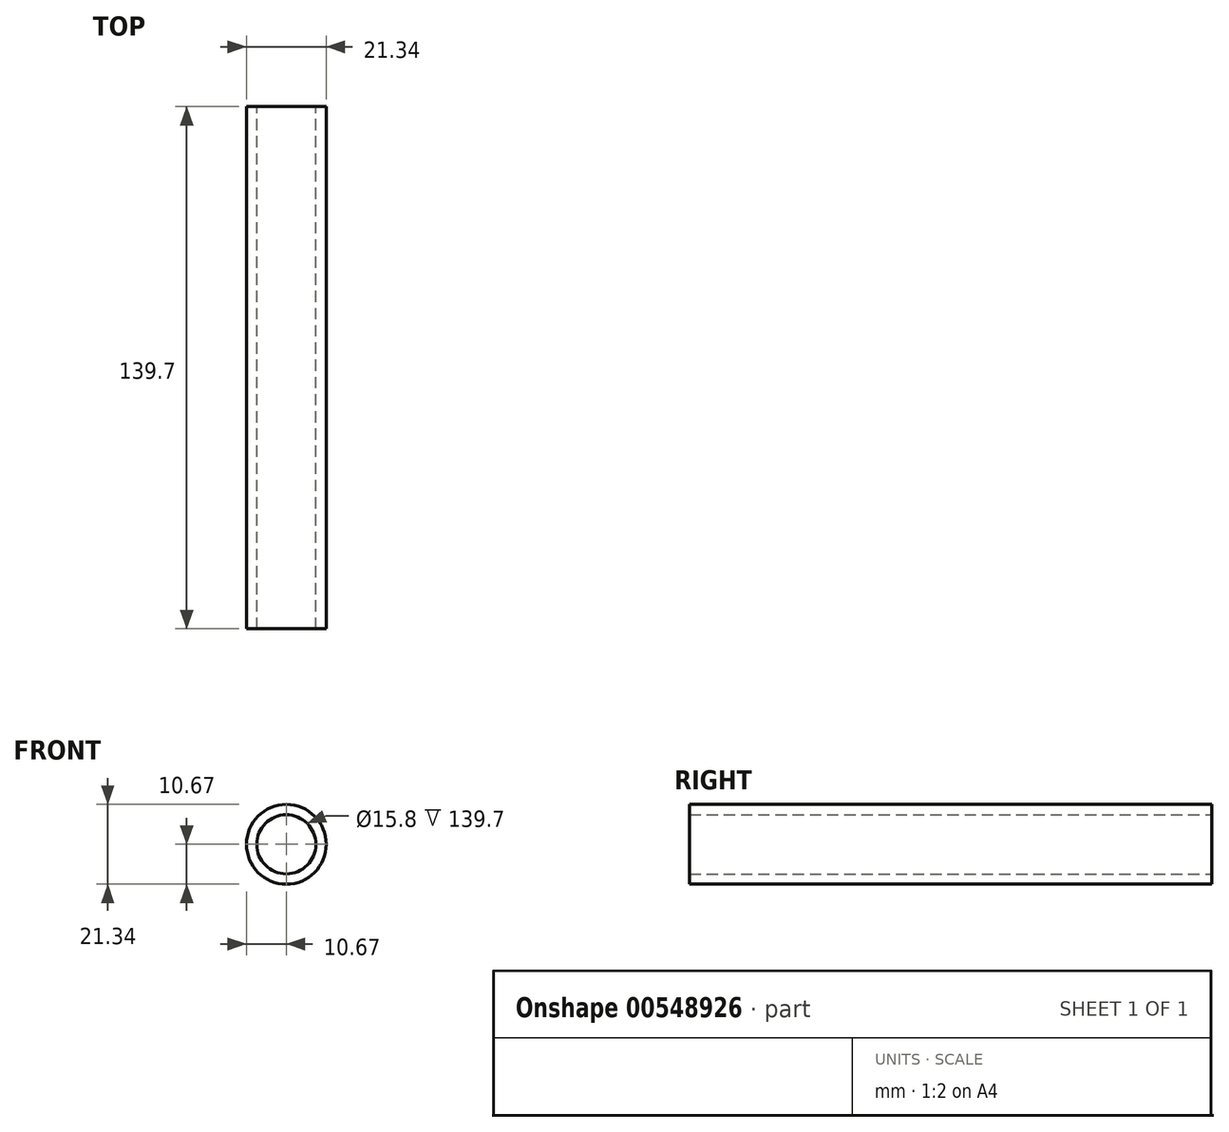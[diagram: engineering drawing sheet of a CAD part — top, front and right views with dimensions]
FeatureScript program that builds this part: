
annotation { "Feature Type Name" : "Feature", "Feature Type Description" : "" }
export const myFeature = defineFeature(function(context is Context, id is Id, definition is map)
    precondition{}
    {
        {
            var Q0;
            Q0=qCreatedBy(makeId("Front.planeOp"),FACE);
            var sketch = newSketch(context, id + "F0", { "sketchPlane" : qUnion([Q0])});
            skCircle(sketch, "E0", {"center": v(0, 0) * mm, "radius": 10.67 * mm});
            skSolve(sketch);
        }
        {
            var Q0;
            Q0=makeQuery(id+"F0.imprint","IMPRINT",FACE,{"disambiguationData":[TD([[makeQuery(id+"F0.imprint","IMPRINT",EDGE,{"derivedFrom":sQuery(id+"F0.wireOp",EDGE,"E0")}),1.0]])]});
            extrude(context, id + "F1", {"entities" : qUnion([Q0]), "depth" : 139.7 * mm, "offsetDistance" : 25.4 * mm});
        }
        {
            var Q0;
            Q0=qCreatedBy(makeId("Front.planeOp"),FACE);
            var sketch = newSketch(context, id + "F2", { "sketchPlane" : qUnion([Q0])});
            skCircle(sketch, "E1", {"center": v(0, 0) * mm, "radius": 7.9 * mm});
            skSolve(sketch);
        }
        {
            var Q0;
            Q0=sQuery(id+"F2.wireOp",VERTEX,"E1.center");
            var Q1;
            Q1=makeQuery(id+"F1.opExtrude","SWEPT_BODY",BODY,{"disambiguationData":[OSD([sQuery(id+"F0.wireOp",EDGE,"E0")])]});
            hole(context, id + "F3", {"style" : HoleStyle.SIMPLE, "endStyle" : HoleEndStyle.THROUGH, "oppositeDirection" : true, "holeDiameter" : 15.8 * mm, "isTappedThrough" : true, "tappedDepth" : 12.7 * mm, "tapClearance" : 3, "locations" : qUnion([Q0]), "scope" : qUnion([Q1])});
        }
    });
